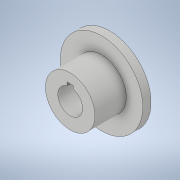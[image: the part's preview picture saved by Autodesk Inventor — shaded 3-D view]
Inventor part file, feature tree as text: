
AUTODESK INVENTOR PART (.ipt)
format: ipt  version: 2021 (Build 250183000, 183)  size: 121,344 bytes
history: native  units: in
note: dims shown in document units (in); Inventor stores cm internally (conversion verified against a paired STEP export)
features: sketch x2, revolve x1, extrude x1
ambient origin geometry x8: Origin, YZ Plane, XZ Plane, XY Plane, X Axis, Y Axis, Z Axis, Center Point
bodies: Solid1 (feature_tree)
feature tree (4):
  revolve  "Revolution1"  [1 undecoded]
  extrude  "Extrusion1"  Depth=0.25in
  sketch  "Sketch1"  dims[d0=0.75in d1=0.95in]
  sketch  "Sketch2"  dims[d2=0.5in d3=0.25in d4=90.0deg d5=0.75in d6=0.188in d7=0.1in d8=0.0in d9=0.0in]
note: 1 required parameter value undecoded (feature->parameter linkage not recoverable at this tier; creation-order binding heuristic only, values carry confidence <= 0.55)
